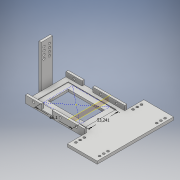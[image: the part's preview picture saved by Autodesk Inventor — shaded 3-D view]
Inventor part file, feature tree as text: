
AUTODESK INVENTOR PART (.ipt)
format: ipt  version: 2018.1 (Build 221171000, 171)  size: 300,544 bytes
history: native  units: mm
features: sketch x11, extrude x10, projected_geometry x4, other x2
ambient origin geometry x8: Origin, YZ Plane, XZ Plane, XY Plane, X Axis, Y Axis, Z Axis, Center Point
bodies: Body1 (feature_tree)
feature tree (27):
  other  "Твердое тело1"
  sketch  "Эскиз1"
  extrude  "Выдавливание1"  Depth=85.0mm
  extrude  "Выдавливание3"  Depth=56.5mm
  extrude  "Выдавливание4"  Depth=9.75mm
  sketch  "Эскиз6"
  extrude  "Выдавливание5"  Depth=68.0mm
  extrude  "Выдавливание6"  Depth=53.0mm
  extrude  "Выдавливание7"  Depth=68.0mm
  extrude  "Выдавливание8"  Depth=5.0mm TaperAngle=0.0deg
  extrude  "Выдавливание9"  Depth=1.0mm TaperAngle=0.0deg
  other  "РабПлоскость1"
  extrude  "Выдавливание10"  Depth=10.25mm
  extrude  "Выдавливание11"  Depth=8.0mm TaperAngle=0.0deg
  sketch  "Эскиз4"
  sketch  "Эскиз5"
  projected_geometry  "Спроецированная петля1"
  sketch  "Эскиз7"
  sketch  "Эскиз8"
  projected_geometry  "Спроецированная петля2"
  sketch  "Эскиз9"
  projected_geometry  "Спроецированная петля3"
  sketch  "Эскиз10"
  sketch  "Эскиз11"
  projected_geometry  "Спроецированная петля4"
  sketch  "Эскиз12"
  sketch  "Эскиз13"
